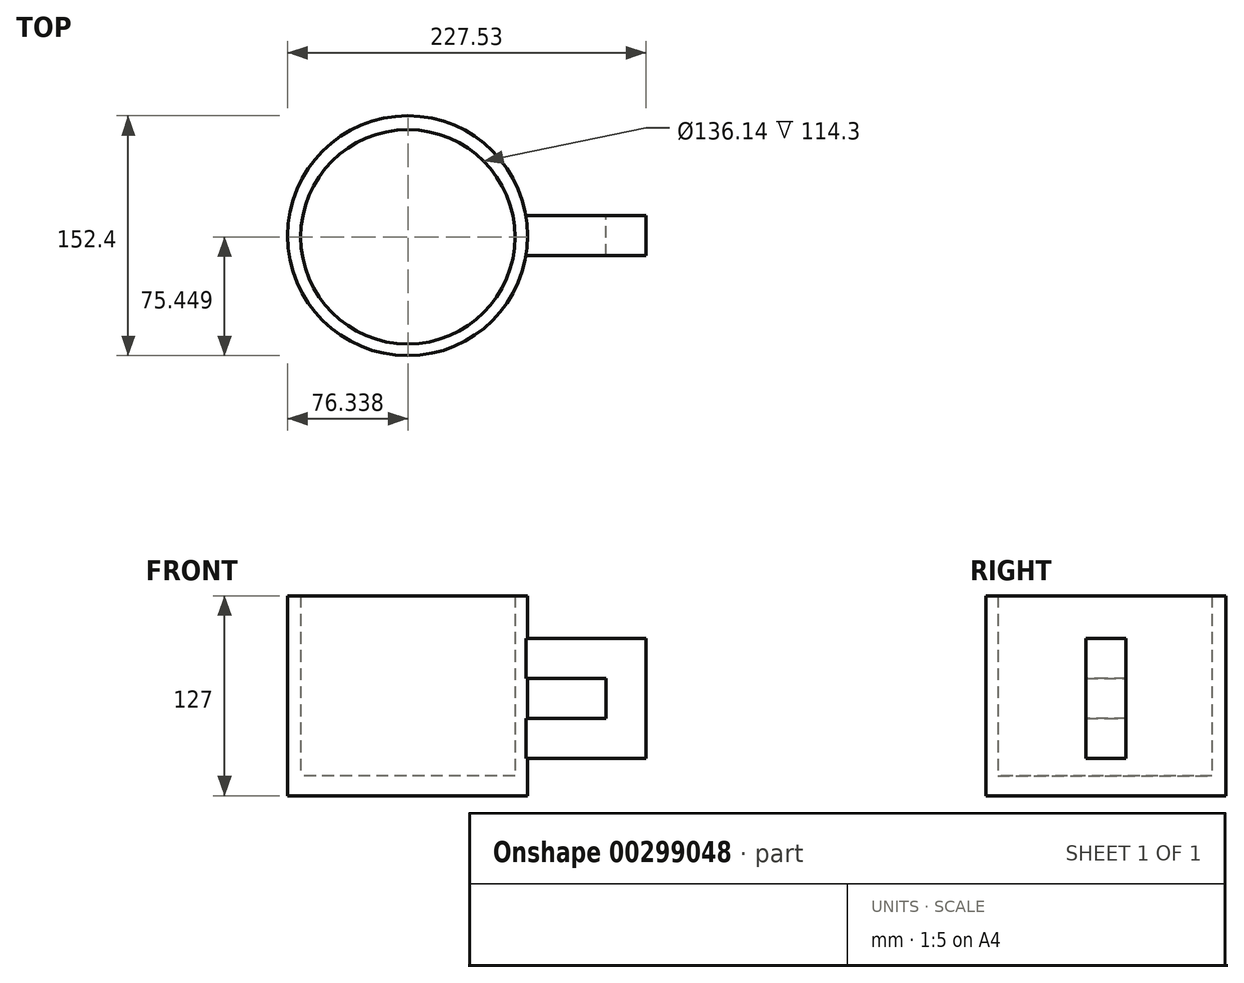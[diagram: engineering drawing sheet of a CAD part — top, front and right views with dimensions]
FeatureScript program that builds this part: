
annotation { "Feature Type Name" : "Feature", "Feature Type Description" : "" }
export const myFeature = defineFeature(function(context is Context, id is Id, definition is map)
    precondition{}
    {
        {
            var Q0;
            Q0=qCreatedBy(makeId("Front.planeOp"),FACE);
            var sketch = newSketch(context, id + "F0", { "sketchPlane" : qUnion([Q0])});
            skLineSegment(sketch, "E0", {"start": v(-41.3, 49.26) * mm, "end": v(34.9, 49.26) * mm});
            skLineSegment(sketch, "E1", {"start": v(34.9, 49.26) * mm, "end": v(34.9, -26.94) * mm});
            skLineSegment(sketch, "E2", {"start": v(34.9, -26.94) * mm, "end": v(-41.3, -26.94) * mm});
            skLineSegment(sketch, "E3.bottom", {"start": v(-41.3, 23.86) * mm, "end": v(9.5, 23.86) * mm});
            skLineSegment(sketch, "E3.top", {"start": v(-41.3, -1.54) * mm, "end": v(9.5, -1.54) * mm});
            skLineSegment(sketch, "E3.right", {"start": v(9.5, 23.86) * mm, "end": v(9.5, -1.54) * mm});
            skLineSegment(sketch, "E4", {"start": v(-41.3, 49.26) * mm, "end": v(-41.3, 23.86) * mm});
            skLineSegment(sketch, "E5", {"start": v(-41.3, -26.94) * mm, "end": v(-41.3, -1.54) * mm});
            skSolve(sketch);
        }
        {
            var Q0;
            Q0=makeQuery(id+"F0.imprint","IMPRINT",FACE,{"disambiguationData":[TD([[makeQuery(id+"F0.imprint","IMPRINT",EDGE,{"derivedFrom":sQuery(id+"F0.wireOp",EDGE,"E0")}),-1.0]])]});
            extrude(context, id + "F1", {"entities" : qUnion([Q0]), "depth" : 25.4 * mm, "hasDraft" : true, "draftAngle" : 0 * degree, "draftPullDirection" : true});
        }
        {
            var Q0;
            Q0=qCreatedBy(makeId("Top.planeOp"),FACE);
            var sketch = newSketch(context, id + "F2", { "sketchPlane" : qUnion([Q0])});
            skCircle(sketch, "E6", {"center": v(-116.43, -12.7) * mm, "radius": 76.2 * mm});
            skPoint(sketch, "E6.first.point", {"position": v(-41.3, 0) * mm});
            skPoint(sketch, "E6.second.point", {"position": v(-41.45, -26.24) * mm});
            skPoint(sketch, "E6.third.point", {"position": v(-190.54, 5.03) * mm});
            skSolve(sketch);
        }
        {
            var Q0;
            Q0=makeQuery(id+"F2.imprint","IMPRINT",FACE,{"disambiguationData":[TD([[makeQuery(id+"F2.imprint","IMPRINT",EDGE,{"derivedFrom":sQuery(id+"F2.wireOp",EDGE,"E6")}),1.0]])]});
            extrude(context, id + "F3", {"entities" : qUnion([Q0]), "operationType" : NewBodyOperationType.ADD, "depth" : 76.2 * mm, "hasSecondDirection" : true, "secondDirectionOppositeDirection" : true, "secondDirectionDepth" : 50.8 * mm});
        }
        {
            var Q0;
            Q0=makeQuery(id+"F3.opExtrude","CAP_FACE",FACE,{"disambiguationData":[OSD([sQuery(id+"F2.wireOp",EDGE,"E6")])],"isStart":false});
            var sketch = newSketch(context, id + "F4", { "sketchPlane" : qUnion([Q0])});
            skSolve(sketch);
        }
        {
            var Q0;
            Q0=makeQuery(id+"F4.imprint","IMPRINT",FACE,{"disambiguationData":[TD([[makeQuery(id+"F4.imprint","IMPRINT",EDGE,{"derivedFrom":makeQuery(id+"F3.opExtrude","CAP_EDGE",EDGE,{"disambiguationData":[OSD([sQuery(id+"F2.wireOp",EDGE,"E6")])],"isStart":false})}),1.0]])]});
            var sketch = newSketch(context, id + "F5", { "sketchPlane" : qUnion([Q0])});
            skCircle(sketch, "E7", {"center": v(-116.3, -13.45) * mm, "radius": 68.07 * mm});
            skSolve(sketch);
        }
        {
            var Q0;
            Q0 = qSketchRegion(id + "F5", true);
            extrude(context, id + "F6", {"entities" : qUnion([Q0]), "operationType" : NewBodyOperationType.REMOVE, "oppositeDirection" : true, "depth" : 114.3 * mm, "hasDraft" : true, "draftAngle" : 0 * degree});
        }
    });
